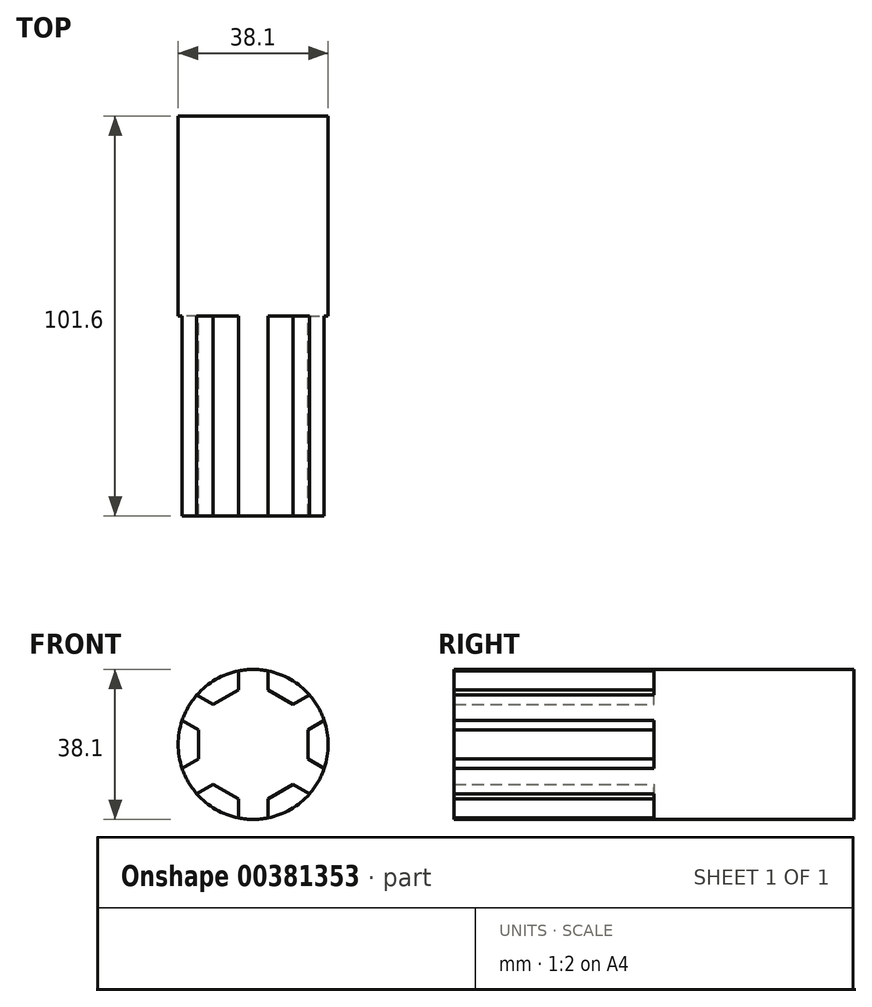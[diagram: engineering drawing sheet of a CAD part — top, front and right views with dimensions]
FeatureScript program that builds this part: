
annotation { "Feature Type Name" : "Feature", "Feature Type Description" : "" }
export const myFeature = defineFeature(function(context is Context, id is Id, definition is map)
    precondition{}
    {
        {
            var Q0;
            Q0=qCreatedBy(makeId("Front.planeOp"),FACE);
            var sketch = newSketch(context, id + "F0", { "sketchPlane" : qUnion([Q0])});
            skCircle(sketch, "E0", {"center": v(0, 0) * mm, "radius": 19.05 * mm});
            skSolve(sketch);
        }
        {
            var Q0;
            Q0 = qSketchRegion(id + "F0", true);
            extrude(context, id + "F1", {"entities" : qUnion([Q0]), "depth" : 50.8 * mm});
        }
        {
            var Q0;
            Q0=makeQuery(id+"F1.opExtrude","CAP_FACE",FACE,{"disambiguationData":[OSD([sQuery(id+"F0.wireOp",EDGE,"E0")])],"isStart":false});
            var sketch = newSketch(context, id + "F2", { "sketchPlane" : qUnion([Q0])});
            skCircle(sketch, "E1.cCircle", {"center": v(0, 0) * mm, "radius": 13.89 * mm, "construction": true});
            skLineSegment(sketch, "E1.0", {"start": v(10.17, -10.17) * mm, "end": v(3.72, -13.89) * mm});
            skLineSegment(sketch, "E1.1", {"start": v(3.72, -13.89) * mm, "end": v(-3.72, -13.89) * mm});
            skLineSegment(sketch, "E1.2", {"start": v(-3.72, -13.89) * mm, "end": v(-10.17, -10.17) * mm});
            skLineSegment(sketch, "E1.3", {"start": v(-10.17, -10.17) * mm, "end": v(-13.89, -3.72) * mm});
            skLineSegment(sketch, "E1.4", {"start": v(-13.89, -3.72) * mm, "end": v(-13.89, 3.72) * mm});
            skLineSegment(sketch, "E1.5", {"start": v(-13.89, 3.72) * mm, "end": v(-10.17, 10.17) * mm});
            skLineSegment(sketch, "E1.6", {"start": v(-10.17, 10.17) * mm, "end": v(-3.72, 13.89) * mm});
            skLineSegment(sketch, "E1.7", {"start": v(-3.72, 13.89) * mm, "end": v(3.72, 13.89) * mm});
            skLineSegment(sketch, "E1.8", {"start": v(3.72, 13.89) * mm, "end": v(10.17, 10.17) * mm});
            skLineSegment(sketch, "E1.9", {"start": v(10.17, 10.17) * mm, "end": v(13.89, 3.72) * mm});
            skLineSegment(sketch, "E1.10", {"start": v(13.89, 3.72) * mm, "end": v(13.89, -3.72) * mm});
            skLineSegment(sketch, "E1.11", {"start": v(13.89, -3.72) * mm, "end": v(10.17, -10.17) * mm});
            skPoint(sketch, "E1.0.midPoint", {"position": v(6.94, -12.03) * mm});
            skLineSegment(sketch, "E2", {"start": v(-3.72, 13.89) * mm, "end": v(-3.72, 18.68) * mm});
            skLineSegment(sketch, "E3", {"start": v(3.72, 13.89) * mm, "end": v(3.72, 18.68) * mm});
            skLineSegment(sketch, "E4", {"start": v(10.17, 10.17) * mm, "end": v(14.32, 12.56) * mm});
            skLineSegment(sketch, "E5", {"start": v(13.89, 3.72) * mm, "end": v(18.04, 6.12) * mm});
            skLineSegment(sketch, "E6", {"start": v(13.89, -3.72) * mm, "end": v(18.04, -6.12) * mm});
            skLineSegment(sketch, "E7", {"start": v(10.17, -10.17) * mm, "end": v(14.32, -12.56) * mm});
            skLineSegment(sketch, "E8", {"start": v(3.72, -13.89) * mm, "end": v(3.72, -18.68) * mm});
            skLineSegment(sketch, "E9", {"start": v(-3.72, -13.89) * mm, "end": v(-3.72, -18.68) * mm});
            skLineSegment(sketch, "E10", {"start": v(-10.17, -10.17) * mm, "end": v(-14.32, -12.56) * mm});
            skLineSegment(sketch, "E11", {"start": v(-13.89, -3.72) * mm, "end": v(-18.04, -6.12) * mm});
            skLineSegment(sketch, "E12", {"start": v(-13.89, 3.72) * mm, "end": v(-18.04, 6.12) * mm});
            skLineSegment(sketch, "E13", {"start": v(-10.17, 10.17) * mm, "end": v(-14.32, 12.56) * mm});
            skSolve(sketch);
        }
        {
            var Q0;
            Q0=makeQuery(id+"F2.imprint","IMPRINT",FACE,{"disambiguationData":[TD([[makeQuery(id+"F2.imprint","IMPRINT",EDGE,{"derivedFrom":sQuery(id+"F2.wireOp",EDGE,"E1.5")}),1.0]])]});
            var Q1;
            Q1=makeQuery(id+"F2.imprint","IMPRINT",FACE,{"disambiguationData":[TD([[makeQuery(id+"F2.imprint","IMPRINT",EDGE,{"derivedFrom":sQuery(id+"F2.wireOp",EDGE,"E1.7")}),1.0]])]});
            var Q2;
            Q2=makeQuery(id+"F2.imprint","IMPRINT",FACE,{"disambiguationData":[TD([[makeQuery(id+"F2.imprint","IMPRINT",EDGE,{"derivedFrom":sQuery(id+"F2.wireOp",EDGE,"E1.9")}),1.0]])]});
            var Q3;
            Q3=makeQuery(id+"F2.imprint","IMPRINT",FACE,{"disambiguationData":[TD([[makeQuery(id+"F2.imprint","IMPRINT",EDGE,{"derivedFrom":sQuery(id+"F2.wireOp",EDGE,"E1.11")}),1.0]])]});
            var Q4;
            Q4=makeQuery(id+"F2.imprint","IMPRINT",FACE,{"disambiguationData":[TD([[makeQuery(id+"F2.imprint","IMPRINT",EDGE,{"derivedFrom":sQuery(id+"F2.wireOp",EDGE,"E1.1")}),1.0]])]});
            var Q5;
            Q5=makeQuery(id+"F2.imprint","IMPRINT",FACE,{"disambiguationData":[TD([[makeQuery(id+"F2.imprint","IMPRINT",EDGE,{"derivedFrom":sQuery(id+"F2.wireOp",EDGE,"E1.3")}),1.0]])]});
            var Q6;
            Q6=makeQuery(id+"F2.imprint","IMPRINT",FACE,{"disambiguationData":[TD([[makeQuery(id+"F2.imprint","IMPRINT",EDGE,{"derivedFrom":sQuery(id+"F2.wireOp",EDGE,"E1.0")}),-1.0]])]});
            extrude(context, id + "F3", {"entities" : qUnion([Q0, Q1, Q2, Q3, Q4, Q5, Q6]), "operationType" : NewBodyOperationType.ADD, "depth" : 50.8 * mm});
        }
    });
